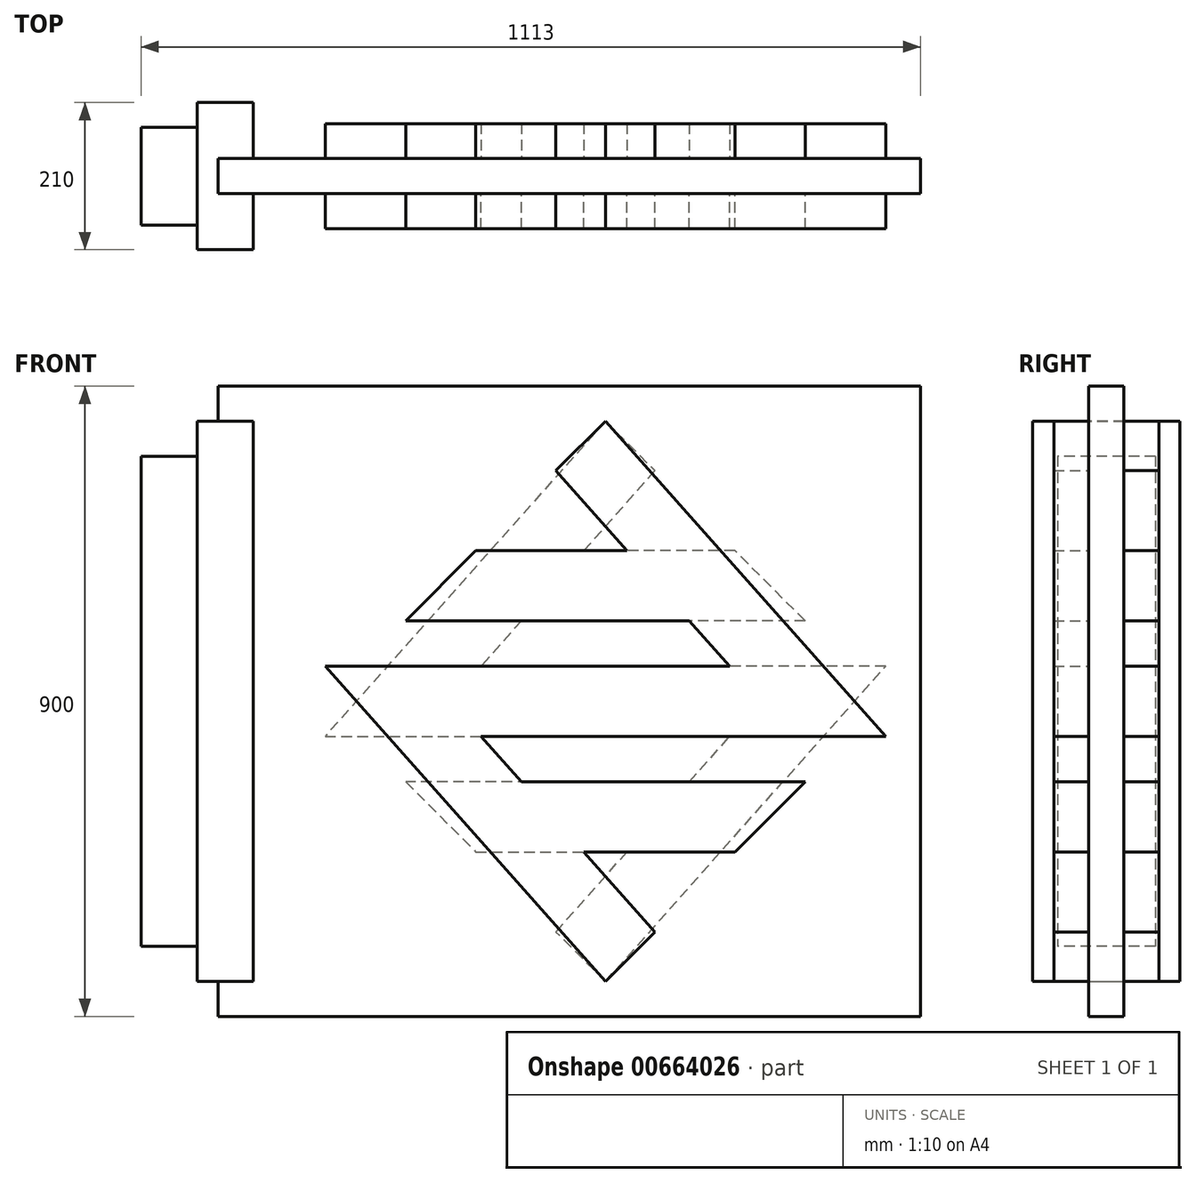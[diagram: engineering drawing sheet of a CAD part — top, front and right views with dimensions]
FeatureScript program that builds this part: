
annotation { "Feature Type Name" : "Feature", "Feature Type Description" : "" }
export const myFeature = defineFeature(function(context is Context, id is Id, definition is map)
    precondition{}
    {
        {
            var Q0;
            Q0=qCreatedBy(makeId("Front.planeOp"),FACE);
            var sketch = newSketch(context, id + "F0", { "sketchPlane" : qUnion([Q0])});
            skLineSegment(sketch, "E0.bottom", {"start": v(-450, 450) * mm, "end": v(450, 450) * mm});
            skLineSegment(sketch, "E0.top", {"start": v(-450, -450) * mm, "end": v(450, -450) * mm});
            skLineSegment(sketch, "E0.left", {"start": v(-450, 450) * mm, "end": v(-450, -450) * mm, "construction": true});
            skLineSegment(sketch, "E0.right", {"start": v(450, 450) * mm, "end": v(450, -450) * mm});
            skPoint(sketch, "E1.firstSnap0", {"position": v(0, -450) * mm});
            skPoint(sketch, "E1.oppositeSnap0", {"position": v(0, -450) * mm});
            skLineSegment(sketch, "E2", {"start": v(-450, 450) * mm, "end": v(-553, 450) * mm});
            skLineSegment(sketch, "E3", {"start": v(-553, 450) * mm, "end": v(-553, -450) * mm});
            skLineSegment(sketch, "E4", {"start": v(-553, -450) * mm, "end": v(-450, -450) * mm});
            skSolve(sketch);
        }
        {
            var Q0;
            Q0=makeQuery(id+"F0.imprint","IMPRINT",FACE,{"disambiguationData":[TD([[makeQuery(id+"F0.imprint","IMPRINT",EDGE,{"derivedFrom":sQuery(id+"F0.wireOp",EDGE,"E0.bottom")}),-1.0]])]});
            extrude(context, id + "F1", {"entities" : qUnion([Q0]), "depth" : 50 * mm, "offsetDistance" : 25 * mm, "symmetric" : true});
        }
        {
            var Q0;
            Q0=makeQuery(id+"F1.opExtrude","CAP_FACE",FACE,{"disambiguationData":[OSD([sQuery(id+"F0.wireOp",EDGE,"E0.bottom"),sQuery(id+"F0.wireOp",EDGE,"E0.top"),sQuery(id+"F0.wireOp",EDGE,"E0.right"),sQuery(id+"F0.wireOp",EDGE,"E2"),sQuery(id+"F0.wireOp",EDGE,"E3"),sQuery(id+"F0.wireOp",EDGE,"E4")])],"isStart":false});
            var sketch = newSketch(context, id + "F2", { "sketchPlane" : qUnion([Q0])});
            skLineSegment(sketch, "E5.bottom", {"start": v(-583, 400) * mm, "end": v(-503, 400) * mm});
            skLineSegment(sketch, "E5.top", {"start": v(-583, -400) * mm, "end": v(-503, -400) * mm});
            skLineSegment(sketch, "E5.left", {"start": v(-583, 400) * mm, "end": v(-583, -400) * mm});
            skLineSegment(sketch, "E5.right", {"start": v(-503, 400) * mm, "end": v(-503, -400) * mm});
            skSolve(sketch);
        }
        {
            var Q0;
            Q0 = qSketchRegion(id + "F2", true);
            extrude(context, id + "F3", {"entities" : qUnion([Q0]), "depth" : 80 * mm, "offsetDistance" : 25 * mm});
        }
        {
            var Q0;
            Q0=makeQuery(id+"F3.opExtrude","SWEPT_BODY",BODY,{"disambiguationData":[OSD([sQuery(id+"F2.wireOp",EDGE,"E5.bottom"),sQuery(id+"F2.wireOp",EDGE,"E5.top"),sQuery(id+"F2.wireOp",EDGE,"E5.left"),sQuery(id+"F2.wireOp",EDGE,"E5.right")])]});
            var Q1;
            Q1=qCreatedBy(makeId("Front.planeOp"),FACE);
            mirror(context, id + "F4", {"entities" : qUnion([Q0]), "mirrorPlane" : qUnion([Q1])});
        }
        {
            var Q0;
            Q0=makeQuery(id+"F4.opPattern","COPY",FACE,{"derivedFrom":makeQuery(id+"F3.opExtrude","SWEPT_FACE",FACE,{"disambiguationData":[OSD([sQuery(id+"F2.wireOp",EDGE,"E5.bottom")])]}),"instanceName":"1"});
            var sketch = newSketch(context, id + "F5", { "sketchPlane" : qUnion([Q0])});
            skLineSegment(sketch, "E6.bottom", {"start": v(-583, 25) * mm, "end": v(-553, 25) * mm});
            skLineSegment(sketch, "E6.top", {"start": v(-583, -25) * mm, "end": v(-553, -25) * mm});
            skLineSegment(sketch, "E6.left", {"start": v(-583, 25) * mm, "end": v(-583, -25) * mm});
            skLineSegment(sketch, "E6.right", {"start": v(-553, 25) * mm, "end": v(-553, -25) * mm});
            skSolve(sketch);
        }
        {
            var Q0;
            Q0 = qSketchRegion(id + "F5", true);
            var Q1;
            Q1=makeQuery(id+"F4.opPattern","COPY",FACE,{"derivedFrom":makeQuery(id+"F3.opExtrude","SWEPT_FACE",FACE,{"disambiguationData":[OSD([sQuery(id+"F2.wireOp",EDGE,"E5.top")])]}),"instanceName":"1"});
            extrude(context, id + "F6", {"entities" : qUnion([Q0]), "operationType" : NewBodyOperationType.ADD, "endBound" : BoundingType.UP_TO_SURFACE, "oppositeDirection" : true, "depth" : 25 * mm, "endBoundEntityFace" : qUnion([Q1]), "offsetDistance" : 25 * mm});
        }
        {
            var Q0;
            Q0=makeQuery(id+"F1.opExtrude","CAP_FACE",FACE,{"disambiguationData":[OSD([sQuery(id+"F0.wireOp",EDGE,"E0.bottom"),sQuery(id+"F0.wireOp",EDGE,"E0.top"),sQuery(id+"F0.wireOp",EDGE,"E0.right"),sQuery(id+"F0.wireOp",EDGE,"E2"),sQuery(id+"F0.wireOp",EDGE,"E3"),sQuery(id+"F0.wireOp",EDGE,"E4")])],"isStart":false});
            var sketch = newSketch(context, id + "F7", { "sketchPlane" : qUnion([Q0])});
            skLineSegment(sketch, "E7.bottom", {"start": v(-400, 400) * mm, "end": v(400, 400) * mm, "construction": true});
            skLineSegment(sketch, "E7.top", {"start": v(-400, -400) * mm, "end": v(400, -400) * mm, "construction": true});
            skLineSegment(sketch, "E7.left", {"start": v(-400, 400) * mm, "end": v(-400, -400) * mm, "construction": true});
            skLineSegment(sketch, "E7.right", {"start": v(400, 400) * mm, "end": v(400, -400) * mm, "construction": true});
            skLineSegment(sketch, "E8", {"start": v(0, 400) * mm, "end": v(0, -400) * mm, "construction": true});
            skLineSegment(sketch, "E9", {"start": v(-400, 0) * mm, "end": v(400, 0) * mm, "construction": true});
            skLineSegment(sketch, "E10", {"start": v(0, -400) * mm, "end": v(-400, 50) * mm});
            skLineSegment(sketch, "E11", {"start": v(0, 400) * mm, "end": v(400, -50) * mm});
            skLineSegment(sketch, "E12", {"start": v(-400, 0) * mm, "end": v(0, 400) * mm, "construction": true});
            skLineSegment(sketch, "E13", {"start": v(0, 400) * mm, "end": v(-70.71, 329.29) * mm});
            skLineSegment(sketch, "E14", {"start": v(-400, 50) * mm, "end": v(177.55, 50) * mm});
            skLineSegment(sketch, "E15", {"start": v(-70.71, 329.29) * mm, "end": v(30.88, 215) * mm});
            skLineSegment(sketch, "E16", {"start": v(400, -50) * mm, "end": v(-177.55, -50) * mm});
            skLineSegment(sketch, "E17", {"start": v(0, -400) * mm, "end": v(400, 0) * mm, "construction": true});
            skLineSegment(sketch, "E18", {"start": v(0, -400) * mm, "end": v(70.71, -329.29) * mm});
            skLineSegment(sketch, "E19", {"start": v(70.71, -329.29) * mm, "end": v(-30.88, -215) * mm});
            skLineSegment(sketch, "E20", {"start": v(-119.77, -115) * mm, "end": v(285, -115) * mm});
            skLineSegment(sketch, "E21", {"start": v(285, -115) * mm, "end": v(185, -215) * mm});
            skLineSegment(sketch, "E22", {"start": v(185, -215) * mm, "end": v(-30.88, -215) * mm});
            skLineSegment(sketch, "E23.trimOffspring", {"start": v(-119.77, -115) * mm, "end": v(-177.55, -50) * mm});
            skLineSegment(sketch, "E24", {"start": v(-285, 115) * mm, "end": v(119.77, 115) * mm});
            skLineSegment(sketch, "E25", {"start": v(-285, 115) * mm, "end": v(-185, 215) * mm});
            skLineSegment(sketch, "E26", {"start": v(-185, 215) * mm, "end": v(30.88, 215) * mm});
            skLineSegment(sketch, "E27.trimOffspring", {"start": v(119.77, 115) * mm, "end": v(177.55, 50) * mm});
            skSolve(sketch);
        }
        {
            var Q0;
            Q0 = qSketchRegion(id + "F7", true);
            extrude(context, id + "F8", {"entities" : qUnion([Q0]), "depth" : 50 * mm, "offsetDistance" : 25 * mm});
        }
        {
            var Q0;
            Q0=makeQuery(id+"F8.opExtrude","SWEPT_BODY",BODY,{"disambiguationData":[OSD([sQuery(id+"F7.wireOp",EDGE,"E10"),sQuery(id+"F7.wireOp",EDGE,"E11"),sQuery(id+"F7.wireOp",EDGE,"E13"),sQuery(id+"F7.wireOp",EDGE,"E14"),sQuery(id+"F7.wireOp",EDGE,"E15"),sQuery(id+"F7.wireOp",EDGE,"E16"),sQuery(id+"F7.wireOp",EDGE,"E18"),sQuery(id+"F7.wireOp",EDGE,"E19"),sQuery(id+"F7.wireOp",EDGE,"E20"),sQuery(id+"F7.wireOp",EDGE,"E21"),sQuery(id+"F7.wireOp",EDGE,"E22"),sQuery(id+"F7.wireOp",EDGE,"E23.trimOffspring"),sQuery(id+"F7.wireOp",EDGE,"E24"),sQuery(id+"F7.wireOp",EDGE,"E25"),sQuery(id+"F7.wireOp",EDGE,"E26"),sQuery(id+"F7.wireOp",EDGE,"E27.trimOffspring")])]});
            var Q1;
            Q1=qCreatedBy(makeId("Front.planeOp"),FACE);
            mirror(context, id + "F9", {"entities" : qUnion([Q0]), "mirrorPlane" : qUnion([Q1])});
        }
        {
            var Q0;
            Q0=makeQuery(id+"F9.opPattern","COPY",BODY,{"derivedFrom":makeQuery(id+"F8.opExtrude","SWEPT_BODY",BODY,{"disambiguationData":[OSD([sQuery(id+"F7.wireOp",EDGE,"E10"),sQuery(id+"F7.wireOp",EDGE,"E11"),sQuery(id+"F7.wireOp",EDGE,"E13"),sQuery(id+"F7.wireOp",EDGE,"E14"),sQuery(id+"F7.wireOp",EDGE,"E15"),sQuery(id+"F7.wireOp",EDGE,"E16"),sQuery(id+"F7.wireOp",EDGE,"E18"),sQuery(id+"F7.wireOp",EDGE,"E19"),sQuery(id+"F7.wireOp",EDGE,"E20"),sQuery(id+"F7.wireOp",EDGE,"E21"),sQuery(id+"F7.wireOp",EDGE,"E22"),sQuery(id+"F7.wireOp",EDGE,"E23.trimOffspring"),sQuery(id+"F7.wireOp",EDGE,"E24"),sQuery(id+"F7.wireOp",EDGE,"E25"),sQuery(id+"F7.wireOp",EDGE,"E26"),sQuery(id+"F7.wireOp",EDGE,"E27.trimOffspring")])]}),"instanceName":"1"});
            var Q1;
            Q1=qCreatedBy(makeId("Right.planeOp"),FACE);
            mirror(context, id + "F10", {"entities" : qUnion([Q0]), "mirrorPlane" : qUnion([Q1])});
        }
        {
            var Q0;
            {var subQ0=makeQuery(id+"F3.opExtrude","SWEPT_FACE",FACE,{"disambiguationData":[OSD([sQuery(id+"F2.wireOp",EDGE,"E5.left")])]});Q0=makeQuery(id+"F6.boolean.opBoolean","MERGE",FACE,{"derivedFrom":[subQ0,makeQuery(id+"F4.opPattern","COPY",FACE,{"derivedFrom":subQ0,"instanceName":"1"}),makeQuery(id+"F6.opExtrude","SWEPT_FACE",FACE,{"disambiguationData":[OSD([sQuery(id+"F5.wireOp",EDGE,"E6.left")])]})]});}
            var sketch = newSketch(context, id + "F11", { "sketchPlane" : qUnion([Q0])});
            skLineSegment(sketch, "E28", {"start": v(0, 400) * mm, "end": v(0, -400) * mm, "construction": true});
            skLineSegment(sketch, "E29.bottom", {"start": v(-70, 350) * mm, "end": v(70, 350) * mm});
            skLineSegment(sketch, "E29.top", {"start": v(-70, -350) * mm, "end": v(70, -350) * mm});
            skLineSegment(sketch, "E29.left", {"start": v(-70, 350) * mm, "end": v(-70, -350) * mm});
            skLineSegment(sketch, "E29.right", {"start": v(70, 350) * mm, "end": v(70, -350) * mm});
            skLineSegment(sketch, "E30", {"start": v(0, 0) * mm, "end": v(-105, 0) * mm, "construction": true});
            skSolve(sketch);
        }
        {
            var Q0;
            Q0 = qSketchRegion(id + "F11", true);
            extrude(context, id + "F12", {"entities" : qUnion([Q0]), "depth" : 80 * mm, "offsetDistance" : 25 * mm});
        }
    });
